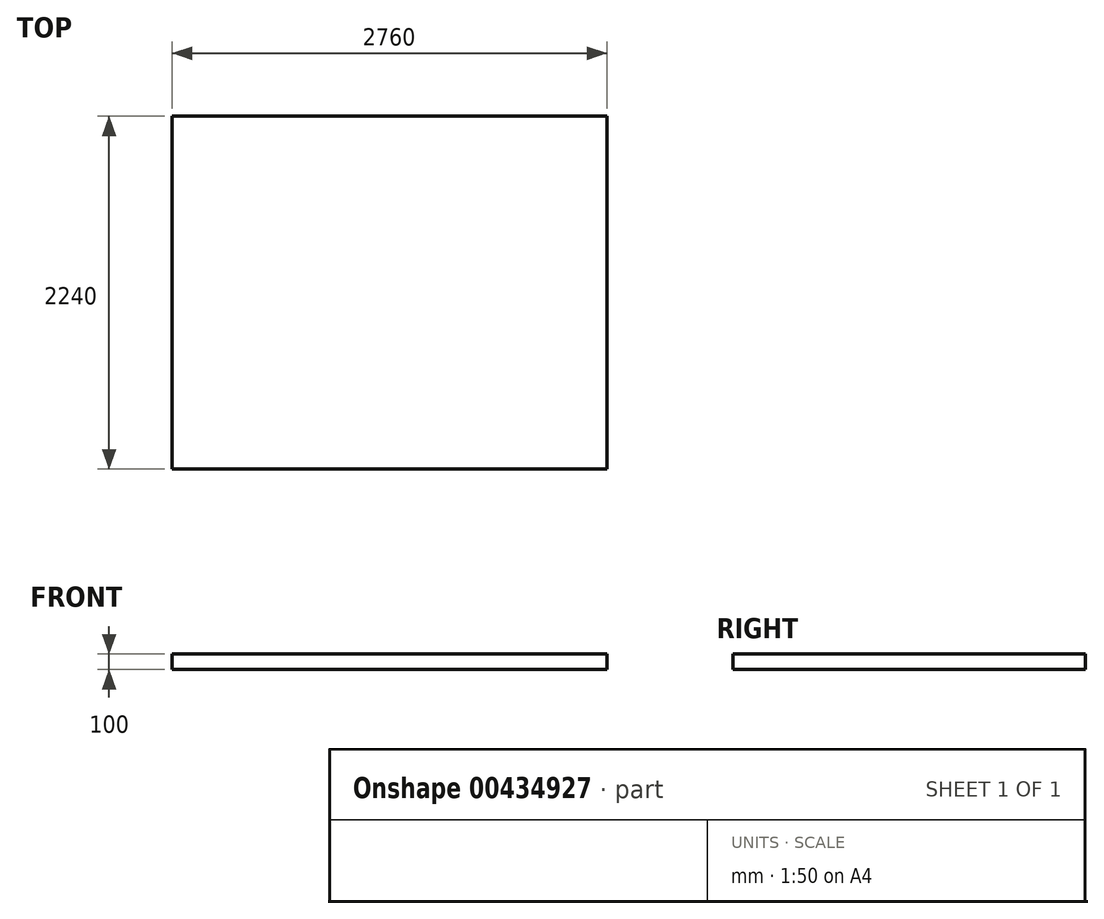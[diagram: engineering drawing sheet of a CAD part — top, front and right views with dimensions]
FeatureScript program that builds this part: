
annotation { "Feature Type Name" : "Feature", "Feature Type Description" : "" }
export const myFeature = defineFeature(function(context is Context, id is Id, definition is map)
    precondition{}
    {
        {
            var Q0;
            Q0=qCreatedBy(makeId("Top.planeOp"),FACE);
            var sketch = newSketch(context, id + "F0", { "sketchPlane" : qUnion([Q0])});
            skLineSegment(sketch, "E0.bottom", {"start": v(1380, 1120) * mm, "end": v(-1380, 1120) * mm});
            skLineSegment(sketch, "E0.top", {"start": v(1380, -1120) * mm, "end": v(-1380, -1120) * mm});
            skLineSegment(sketch, "E0.left", {"start": v(1380, 1120) * mm, "end": v(1380, -1120) * mm});
            skLineSegment(sketch, "E0.right", {"start": v(-1380, 1120) * mm, "end": v(-1380, -1120) * mm});
            skPoint(sketch, "E0.middle", {"position": v(0, 0) * mm});
            skSolve(sketch);
        }
        {
            var Q0;
            Q0 = qSketchRegion(id + "F0", true);
            extrude(context, id + "F1", {"entities" : qUnion([Q0]), "depth" : 100 * mm});
        }
    });
